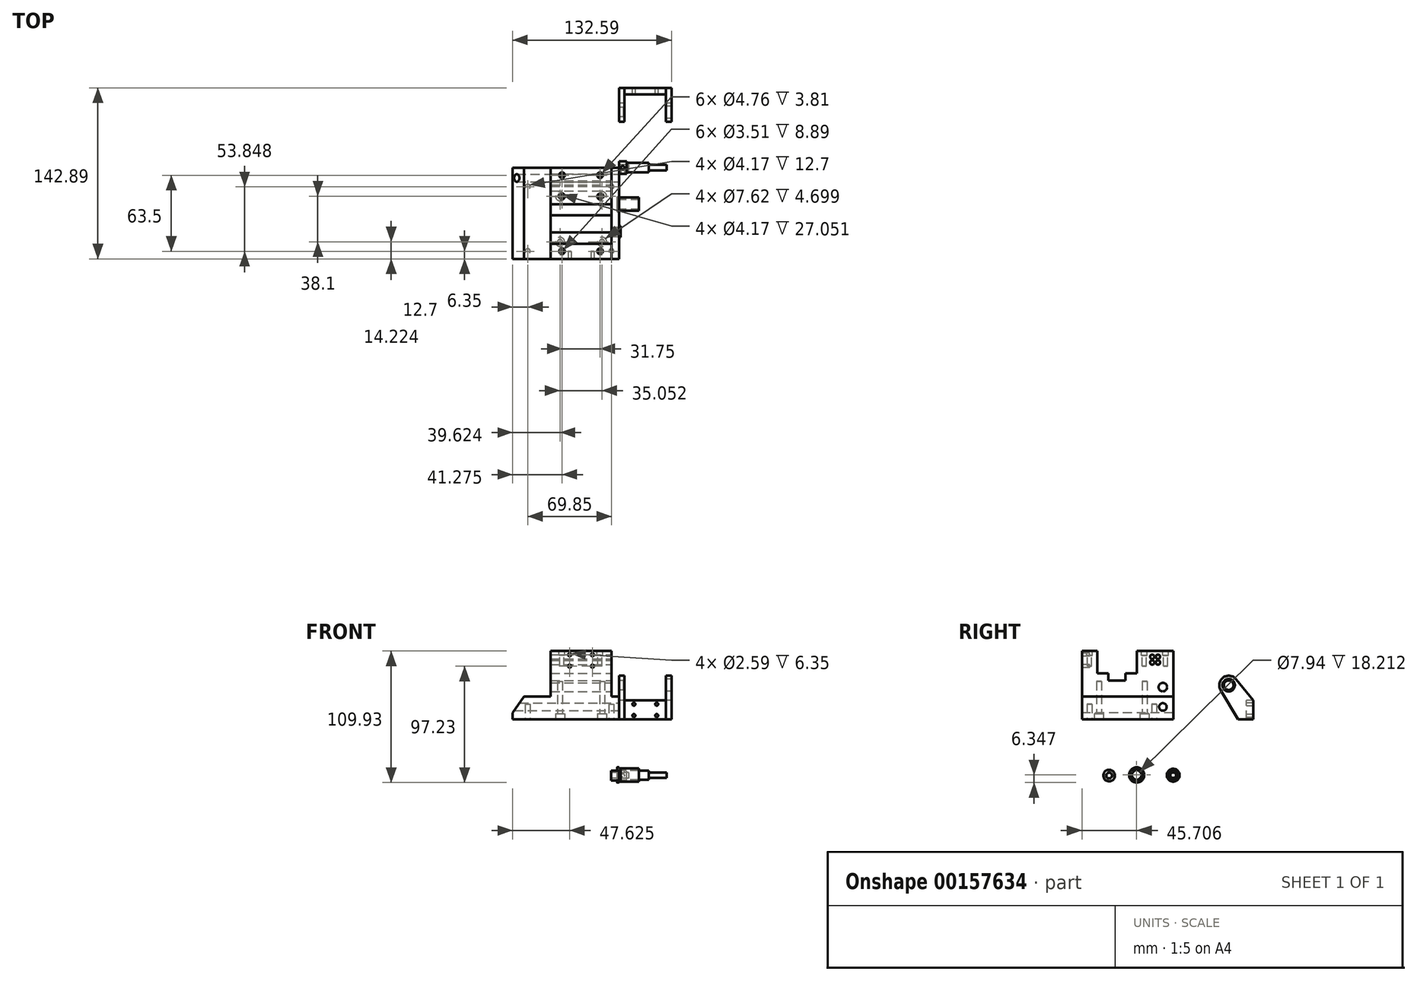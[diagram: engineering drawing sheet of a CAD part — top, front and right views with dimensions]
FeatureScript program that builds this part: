
annotation { "Feature Type Name" : "Feature", "Feature Type Description" : "" }
export const myFeature = defineFeature(function(context is Context, id is Id, definition is map)
    precondition{}
    {
        {
            var Q0;
            Q0=qCreatedBy(makeId("Top.planeOp"),FACE);
            var sketch = newSketch(context, id + "F0", { "sketchPlane" : qUnion([Q0])});
            skLineSegment(sketch, "E0.bottom", {"start": v(0, 0) * mm, "end": v(-88.9, 0) * mm});
            skLineSegment(sketch, "E0.top", {"start": v(0, -76.2) * mm, "end": v(-88.9, -76.2) * mm});
            skLineSegment(sketch, "E0.left", {"start": v(0, 0) * mm, "end": v(0, -76.2) * mm});
            skLineSegment(sketch, "E0.right", {"start": v(-88.9, 0) * mm, "end": v(-88.9, -76.2) * mm});
            skSolve(sketch);
        }
        {
            var Q0;
            Q0=makeQuery(id+"F0.imprint","IMPRINT",FACE,{"disambiguationData":[TD([[makeQuery(id+"F0.imprint","IMPRINT",EDGE,{"derivedFrom":sQuery(id+"F0.wireOp",EDGE,"E0.bottom")}),1.0]])]});
            extrude(context, id + "F1", {"entities" : qUnion([Q0]), "depth" : 19.05 * mm});
        }
        {
            var Q0;
            Q0=makeQuery(id+"F1.opExtrude","CAP_FACE",FACE,{"disambiguationData":[OSD([sQuery(id+"F0.wireOp",EDGE,"E0.bottom"),sQuery(id+"F0.wireOp",EDGE,"E0.top"),sQuery(id+"F0.wireOp",EDGE,"E0.left"),sQuery(id+"F0.wireOp",EDGE,"E0.right")])],"isStart":false});
            var sketch = newSketch(context, id + "F2", { "sketchPlane" : qUnion([Q0])});
            skLineSegment(sketch, "E1", {"start": v(0, 0) * mm, "end": v(-6.35, 0) * mm, "construction": true});
            skLineSegment(sketch, "E2.bottom", {"start": v(-6.35, 0) * mm, "end": v(-57.15, 0) * mm});
            skLineSegment(sketch, "E2.top", {"start": v(-6.35, -76.2) * mm, "end": v(-57.15, -76.2) * mm});
            skLineSegment(sketch, "E2.left", {"start": v(-6.35, 0) * mm, "end": v(-6.35, -76.2) * mm});
            skLineSegment(sketch, "E2.right", {"start": v(-57.15, 0) * mm, "end": v(-57.15, -76.2) * mm});
            skSolve(sketch);
        }
        {
            var Q0;
            Q0=makeQuery(id+"F2.imprint","IMPRINT",FACE,{"disambiguationData":[TD([[makeQuery(id+"F2.imprint","IMPRINT",EDGE,{"derivedFrom":sQuery(id+"F2.wireOp",EDGE,"E2.bottom")}),1.0]])]});
            extrude(context, id + "F3", {"entities" : qUnion([Q0]), "operationType" : NewBodyOperationType.ADD, "depth" : 38.1 * mm});
        }
        {
            var Q0;
            Q0=makeQuery(id+"F3.opExtrude","SWEPT_FACE",FACE,{"disambiguationData":[OSD([sQuery(id+"F2.wireOp",EDGE,"E2.left")])]});
            var sketch = newSketch(context, id + "F4", { "sketchPlane" : qUnion([Q0])});
            skLineSegment(sketch, "E3", {"start": v(-76.2, 57.15) * mm, "end": v(-63.5, 57.15) * mm, "construction": true});
            skLineSegment(sketch, "E4", {"start": v(-54.1, 38.6) * mm, "end": v(-54.1, 35.05) * mm});
            skLineSegment(sketch, "E5", {"start": v(-51.56, 32.51) * mm, "end": v(-42.42, 32.51) * mm});
            skLineSegment(sketch, "E6", {"start": v(-39.88, 35.05) * mm, "end": v(-39.88, 38.6) * mm});
            skLineSegment(sketch, "E7", {"start": v(-30.48, 41.4) * mm, "end": v(-30.48, 57.15) * mm});
            skPoint(sketch, "E8.visualSharp", {"position": v(-54.1, 32.51) * mm});
            skPoint(sketch, "E9.visualSharp", {"position": v(-39.88, 32.51) * mm});
            skLineSegment(sketch, "E10", {"start": v(-63.5, 57.15) * mm, "end": v(-63.5, 41.15) * mm});
            skLineSegment(sketch, "E11", {"start": v(-60.96, 38.6) * mm, "end": v(-54.1, 38.6) * mm});
            skLineSegment(sketch, "E12", {"start": v(-39.88, 38.6) * mm, "end": v(-33.02, 38.6) * mm});
            skLineSegment(sketch, "E13", {"start": v(-30.48, 41.15) * mm, "end": v(-30.48, 41.4) * mm});
            skPoint(sketch, "E14.visualSharp", {"position": v(-63.5, 38.6) * mm});
            skPoint(sketch, "E15.visualSharp", {"position": v(-30.48, 38.6) * mm});
            skLineSegment(sketch, "E16", {"start": v(-33.02, 38.6) * mm, "end": v(-30.48, 38.6) * mm});
            skLineSegment(sketch, "E17", {"start": v(-30.48, 41.15) * mm, "end": v(-30.48, 38.6) * mm});
            skLineSegment(sketch, "E18", {"start": v(-60.96, 38.6) * mm, "end": v(-63.5, 38.6) * mm});
            skLineSegment(sketch, "E19", {"start": v(-63.5, 41.15) * mm, "end": v(-63.5, 38.6) * mm});
            skLineSegment(sketch, "E20", {"start": v(-54.1, 35.05) * mm, "end": v(-54.1, 32.51) * mm});
            skLineSegment(sketch, "E21", {"start": v(-51.56, 32.51) * mm, "end": v(-54.1, 32.51) * mm});
            skLineSegment(sketch, "E22", {"start": v(-42.42, 32.51) * mm, "end": v(-39.88, 32.51) * mm});
            skLineSegment(sketch, "E23", {"start": v(-39.88, 32.51) * mm, "end": v(-39.88, 35.05) * mm});
            skSolve(sketch);
        }
        {
            var Q0;
            Q0=makeQuery(id+"F4.imprint","IMPRINT",FACE,{"disambiguationData":[TD([[makeQuery(id+"F4.imprint","IMPRINT",EDGE,{"derivedFrom":sQuery(id+"F4.wireOp",EDGE,"E4")}),1.0]])]});
            extrude(context, id + "F5", {"entities" : qUnion([Q0]), "operationType" : NewBodyOperationType.REMOVE, "endBound" : BoundingType.THROUGH_ALL, "oppositeDirection" : true, "depth" : 25.4 * mm});
        }
        {
            var Q0;
            Q0=makeQuery(id+"F3.boolean.opBoolean","MERGE",FACE,{"derivedFrom":[makeQuery(id+"F1.opExtrude","SWEPT_FACE",FACE,{"disambiguationData":[OSD([sQuery(id+"F0.wireOp",EDGE,"E0.top")])]}),makeQuery(id+"F3.opExtrude","SWEPT_FACE",FACE,{"disambiguationData":[OSD([sQuery(id+"F2.wireOp",EDGE,"E2.top")])]})]});
            var sketch = newSketch(context, id + "F6", { "sketchPlane" : qUnion([Q0])});
            skLineSegment(sketch, "E24", {"start": v(-88.9, 5.34) * mm, "end": v(-79.3, 19.05) * mm});
            skSolve(sketch);
        }
        {
            var Q0;
            {var subQ0=sQuery(id+"F6.wireOp",EDGE,"E24");Q0=makeQuery(id+"F6.imprint","IMPRINT",FACE,{"disambiguationData":[TD([[makeQuery(id+"F6.imprint","IMPRINT",EDGE,{"derivedFrom":subQ0}),1.0]])]});}
            extrude(context, id + "F7", {"entities" : qUnion([Q0]), "operationType" : NewBodyOperationType.REMOVE, "endBound" : BoundingType.THROUGH_ALL, "oppositeDirection" : true, "depth" : 25.4 * mm});
        }
        {
            var Q0;
            Q0=makeQuery(id+"F1.opExtrude","SWEPT_FACE",FACE,{"disambiguationData":[OSD([sQuery(id+"F0.wireOp",EDGE,"E0.left")])]});
            var sketch = newSketch(context, id + "F8", { "sketchPlane" : qUnion([Q0])});
            skCircle(sketch, "E25", {"center": v(-8.64, 10.41) * mm, "radius": 3.18 * mm});
            skSolve(sketch);
        }
        {
            var Q0;
            Q0=makeQuery(id+"F8.imprint","IMPRINT",FACE,{"disambiguationData":[TD([[makeQuery(id+"F8.imprint","IMPRINT",EDGE,{"derivedFrom":sQuery(id+"F8.wireOp",EDGE,"E25")}),1.0]])]});
            extrude(context, id + "F9", {"entities" : qUnion([Q0]), "operationType" : NewBodyOperationType.REMOVE, "endBound" : BoundingType.THROUGH_ALL, "oppositeDirection" : true, "depth" : 25.4 * mm});
        }
        {
            var Q0;
            Q0=makeQuery(id+"F3.opExtrude","SWEPT_FACE",FACE,{"disambiguationData":[OSD([sQuery(id+"F2.wireOp",EDGE,"E2.left")])]});
            var sketch = newSketch(context, id + "F10", { "sketchPlane" : qUnion([Q0])});
            skCircle(sketch, "E26", {"center": v(-8.64, 26.92) * mm, "radius": 3.56 * mm});
            skSolve(sketch);
        }
        {
            var Q0;
            Q0=makeQuery(id+"F10.imprint","IMPRINT",FACE,{"disambiguationData":[TD([[makeQuery(id+"F10.imprint","IMPRINT",EDGE,{"derivedFrom":sQuery(id+"F10.wireOp",EDGE,"E26")}),1.0]])]});
            extrude(context, id + "F11", {"entities" : qUnion([Q0]), "operationType" : NewBodyOperationType.REMOVE, "endBound" : BoundingType.THROUGH_ALL, "oppositeDirection" : true, "depth" : 25.4 * mm});
        }
        {
            var Q0;
            Q0=makeQuery(id+"F3.opExtrude","SWEPT_FACE",FACE,{"disambiguationData":[OSD([sQuery(id+"F2.wireOp",EDGE,"E2.left")])]});
            var sketch = newSketch(context, id + "F12", { "sketchPlane" : qUnion([Q0])});
            skLineSegment(sketch, "E27.bottom", {"start": v(-17.53, 52.32) * mm, "end": v(-12.7, 52.32) * mm, "construction": true});
            skLineSegment(sketch, "E27.top", {"start": v(-17.53, 47.5) * mm, "end": v(-12.7, 47.5) * mm, "construction": true});
            skLineSegment(sketch, "E27.left", {"start": v(-17.53, 52.32) * mm, "end": v(-17.53, 47.5) * mm, "construction": true});
            skLineSegment(sketch, "E27.right", {"start": v(-12.7, 52.32) * mm, "end": v(-12.7, 47.5) * mm, "construction": true});
            skCircle(sketch, "E28", {"center": v(-12.7, 52.32) * mm, "radius": 1.83 * mm});
            skCircle(sketch, "E29", {"center": v(-17.53, 52.32) * mm, "radius": 1.83 * mm});
            skCircle(sketch, "E30", {"center": v(-17.53, 47.5) * mm, "radius": 1.83 * mm});
            skCircle(sketch, "E31", {"center": v(-12.7, 47.5) * mm, "radius": 1.83 * mm});
            skSolve(sketch);
        }
        {
            var Q0;
            Q0=makeQuery(id+"F12.imprint","IMPRINT",FACE,{"disambiguationData":[TD([[makeQuery(id+"F12.imprint","IMPRINT",EDGE,{"derivedFrom":sQuery(id+"F12.wireOp",EDGE,"E30")}),1.0]])]});
            var Q1;
            Q1=makeQuery(id+"F12.imprint","IMPRINT",FACE,{"disambiguationData":[TD([[makeQuery(id+"F12.imprint","IMPRINT",EDGE,{"derivedFrom":sQuery(id+"F12.wireOp",EDGE,"E31")}),1.0]])]});
            var Q2;
            Q2=makeQuery(id+"F12.imprint","IMPRINT",FACE,{"disambiguationData":[TD([[makeQuery(id+"F12.imprint","IMPRINT",EDGE,{"derivedFrom":sQuery(id+"F12.wireOp",EDGE,"E28")}),1.0]])]});
            var Q3;
            Q3=makeQuery(id+"F12.imprint","IMPRINT",FACE,{"disambiguationData":[TD([[makeQuery(id+"F12.imprint","IMPRINT",EDGE,{"derivedFrom":sQuery(id+"F12.wireOp",EDGE,"E29")}),1.0]])]});
            extrude(context, id + "F13", {"entities" : qUnion([Q0, Q1, Q2, Q3]), "operationType" : NewBodyOperationType.REMOVE, "endBound" : BoundingType.THROUGH_ALL, "oppositeDirection" : true, "depth" : 25.4 * mm});
        }
        {
            var Q0;
            Q0=makeQuery(id+"F1.opExtrude","CAP_FACE",FACE,{"disambiguationData":[OSD([sQuery(id+"F0.wireOp",EDGE,"E0.bottom"),sQuery(id+"F0.wireOp",EDGE,"E0.top"),sQuery(id+"F0.wireOp",EDGE,"E0.left"),sQuery(id+"F0.wireOp",EDGE,"E0.right")])],"isStart":true});
            var sketch = newSketch(context, id + "F14", { "sketchPlane" : qUnion([Q0])});
            skLineSegment(sketch, "E32.bottom", {"start": v(-76.2, 69.85) * mm, "end": v(-6.35, 69.85) * mm, "construction": true});
            skLineSegment(sketch, "E32.top", {"start": v(-76.2, 16) * mm, "end": v(-6.35, 16) * mm, "construction": true});
            skLineSegment(sketch, "E32.left", {"start": v(-76.2, 69.85) * mm, "end": v(-76.2, 16) * mm, "construction": true});
            skLineSegment(sketch, "E32.right", {"start": v(-6.35, 69.85) * mm, "end": v(-6.35, 16) * mm, "construction": true});
            skCircle(sketch, "E33", {"center": v(-6.35, 69.85) * mm, "radius": 2.08 * mm});
            skCircle(sketch, "E34", {"center": v(-76.2, 69.85) * mm, "radius": 2.08 * mm});
            skCircle(sketch, "E35", {"center": v(-76.2, 16) * mm, "radius": 2.08 * mm});
            skCircle(sketch, "E36", {"center": v(-6.35, 16) * mm, "radius": 2.08 * mm});
            skSolve(sketch);
        }
        {
            var Q0;
            Q0=makeQuery(id+"F14.imprint","IMPRINT",FACE,{"disambiguationData":[TD([[makeQuery(id+"F14.imprint","IMPRINT",EDGE,{"derivedFrom":sQuery(id+"F14.wireOp",EDGE,"E34")}),1.0]])]});
            var Q1;
            Q1=makeQuery(id+"F14.imprint","IMPRINT",FACE,{"disambiguationData":[TD([[makeQuery(id+"F14.imprint","IMPRINT",EDGE,{"derivedFrom":sQuery(id+"F14.wireOp",EDGE,"E33")}),1.0]])]});
            var Q2;
            Q2=makeQuery(id+"F14.imprint","IMPRINT",FACE,{"disambiguationData":[TD([[makeQuery(id+"F14.imprint","IMPRINT",EDGE,{"derivedFrom":sQuery(id+"F14.wireOp",EDGE,"E35")}),1.0]])]});
            var Q3;
            Q3=makeQuery(id+"F14.imprint","IMPRINT",FACE,{"disambiguationData":[TD([[makeQuery(id+"F14.imprint","IMPRINT",EDGE,{"derivedFrom":sQuery(id+"F14.wireOp",EDGE,"E36")}),1.0]])]});
            extrude(context, id + "F15", {"entities" : qUnion([Q0, Q1, Q2, Q3]), "operationType" : NewBodyOperationType.REMOVE, "oppositeDirection" : true, "depth" : 12.7 * mm});
        }
        {
            var Q0;
            Q0=makeQuery(id+"F1.opExtrude","CAP_FACE",FACE,{"disambiguationData":[OSD([sQuery(id+"F0.wireOp",EDGE,"E0.bottom"),sQuery(id+"F0.wireOp",EDGE,"E0.top"),sQuery(id+"F0.wireOp",EDGE,"E0.left"),sQuery(id+"F0.wireOp",EDGE,"E0.right")])],"isStart":true});
            var sketch = newSketch(context, id + "F16", { "sketchPlane" : qUnion([Q0])});
            skLineSegment(sketch, "E37.bottom", {"start": v(-49.28, 61.98) * mm, "end": v(-14.22, 61.98) * mm, "construction": true});
            skLineSegment(sketch, "E37.top", {"start": v(-49.28, 23.88) * mm, "end": v(-14.22, 23.88) * mm, "construction": true});
            skLineSegment(sketch, "E37.left", {"start": v(-49.28, 61.98) * mm, "end": v(-49.28, 23.88) * mm, "construction": true});
            skLineSegment(sketch, "E37.right", {"start": v(-14.22, 61.98) * mm, "end": v(-14.22, 23.88) * mm, "construction": true});
            skCircle(sketch, "E38", {"center": v(-14.22, 61.98) * mm, "radius": 2.08 * mm});
            skCircle(sketch, "E39", {"center": v(-49.28, 61.98) * mm, "radius": 2.08 * mm});
            skCircle(sketch, "E40", {"center": v(-49.28, 23.88) * mm, "radius": 2.08 * mm});
            skCircle(sketch, "E41", {"center": v(-14.22, 23.88) * mm, "radius": 2.08 * mm});
            skCircle(sketch, "E42", {"center": v(-14.22, 61.98) * mm, "radius": 3.81 * mm});
            skCircle(sketch, "E43", {"center": v(-49.28, 61.98) * mm, "radius": 3.81 * mm});
            skCircle(sketch, "E44", {"center": v(-49.28, 23.88) * mm, "radius": 3.81 * mm});
            skCircle(sketch, "E45", {"center": v(-14.22, 23.88) * mm, "radius": 3.81 * mm});
            skSolve(sketch);
        }
        {
            var Q0;
            Q0=makeQuery(id+"F16.imprint","IMPRINT",FACE,{"disambiguationData":[TD([[makeQuery(id+"F16.imprint","IMPRINT",EDGE,{"derivedFrom":sQuery(id+"F16.wireOp",EDGE,"E39")}),1.0]])]});
            var Q1;
            Q1=makeQuery(id+"F16.imprint","IMPRINT",FACE,{"disambiguationData":[TD([[makeQuery(id+"F16.imprint","IMPRINT",EDGE,{"derivedFrom":sQuery(id+"F16.wireOp",EDGE,"E38")}),1.0]])]});
            var Q2;
            Q2=makeQuery(id+"F16.imprint","IMPRINT",FACE,{"disambiguationData":[TD([[makeQuery(id+"F16.imprint","IMPRINT",EDGE,{"derivedFrom":sQuery(id+"F16.wireOp",EDGE,"E41")}),1.0]])]});
            var Q3;
            Q3=makeQuery(id+"F16.imprint","IMPRINT",FACE,{"disambiguationData":[TD([[makeQuery(id+"F16.imprint","IMPRINT",EDGE,{"derivedFrom":sQuery(id+"F16.wireOp",EDGE,"E40")}),1.0]])]});
            extrude(context, id + "F17", {"entities" : qUnion([Q0, Q1, Q2, Q3]), "operationType" : NewBodyOperationType.REMOVE, "oppositeDirection" : true, "depth" : 31.75 * mm});
        }
        {
            var Q0;
            Q0=makeQuery(id+"F16.imprint","IMPRINT",FACE,{"disambiguationData":[TD([[makeQuery(id+"F16.imprint","IMPRINT",EDGE,{"derivedFrom":sQuery(id+"F16.wireOp",EDGE,"E39")}),-1.0]])]});
            var Q1;
            Q1=makeQuery(id+"F16.imprint","IMPRINT",FACE,{"disambiguationData":[TD([[makeQuery(id+"F16.imprint","IMPRINT",EDGE,{"derivedFrom":sQuery(id+"F16.wireOp",EDGE,"E38")}),-1.0]])]});
            var Q2;
            Q2=makeQuery(id+"F16.imprint","IMPRINT",FACE,{"disambiguationData":[TD([[makeQuery(id+"F16.imprint","IMPRINT",EDGE,{"derivedFrom":sQuery(id+"F16.wireOp",EDGE,"E41")}),-1.0]])]});
            var Q3;
            Q3=makeQuery(id+"F16.imprint","IMPRINT",FACE,{"disambiguationData":[TD([[makeQuery(id+"F16.imprint","IMPRINT",EDGE,{"derivedFrom":sQuery(id+"F16.wireOp",EDGE,"E40")}),-1.0]])]});
            extrude(context, id + "F18", {"entities" : qUnion([Q0, Q1, Q2, Q3]), "operationType" : NewBodyOperationType.REMOVE, "oppositeDirection" : true, "depth" : 4.7 * mm});
        }
        {
            var Q0;
            Q0=makeQuery(id+"F3.boolean.opBoolean","MERGE",FACE,{"derivedFrom":[makeQuery(id+"F1.opExtrude","SWEPT_FACE",FACE,{"disambiguationData":[OSD([sQuery(id+"F0.wireOp",EDGE,"E0.top")])]}),makeQuery(id+"F3.opExtrude","SWEPT_FACE",FACE,{"disambiguationData":[OSD([sQuery(id+"F2.wireOp",EDGE,"E2.top")])]})]});
            var sketch = newSketch(context, id + "F19", { "sketchPlane" : qUnion([Q0])});
            skLineSegment(sketch, "E46.bottom", {"start": v(-41.28, 53.98) * mm, "end": v(-22.23, 53.98) * mm, "construction": true});
            skLineSegment(sketch, "E46.top", {"start": v(-41.28, 44.45) * mm, "end": v(-22.23, 44.45) * mm, "construction": true});
            skLineSegment(sketch, "E46.left", {"start": v(-41.28, 53.98) * mm, "end": v(-41.28, 44.45) * mm, "construction": true});
            skLineSegment(sketch, "E46.right", {"start": v(-22.23, 53.98) * mm, "end": v(-22.23, 44.45) * mm, "construction": true});
            skCircle(sketch, "E47", {"center": v(-22.23, 53.98) * mm, "radius": 1.3 * mm});
            skCircle(sketch, "E48", {"center": v(-41.28, 53.98) * mm, "radius": 1.3 * mm});
            skCircle(sketch, "E49", {"center": v(-41.28, 44.45) * mm, "radius": 1.3 * mm});
            skCircle(sketch, "E50", {"center": v(-22.23, 44.45) * mm, "radius": 1.3 * mm});
            skSolve(sketch);
        }
        {
            var Q0;
            Q0=makeQuery(id+"F19.imprint","IMPRINT",FACE,{"disambiguationData":[TD([[makeQuery(id+"F19.imprint","IMPRINT",EDGE,{"derivedFrom":sQuery(id+"F19.wireOp",EDGE,"E49")}),1.0]])]});
            var Q1;
            Q1=makeQuery(id+"F19.imprint","IMPRINT",FACE,{"disambiguationData":[TD([[makeQuery(id+"F19.imprint","IMPRINT",EDGE,{"derivedFrom":sQuery(id+"F19.wireOp",EDGE,"E48")}),1.0]])]});
            var Q2;
            Q2=makeQuery(id+"F19.imprint","IMPRINT",FACE,{"disambiguationData":[TD([[makeQuery(id+"F19.imprint","IMPRINT",EDGE,{"derivedFrom":sQuery(id+"F19.wireOp",EDGE,"E47")}),1.0]])]});
            var Q3;
            Q3=makeQuery(id+"F19.imprint","IMPRINT",FACE,{"disambiguationData":[TD([[makeQuery(id+"F19.imprint","IMPRINT",EDGE,{"derivedFrom":sQuery(id+"F19.wireOp",EDGE,"E50")}),1.0]])]});
            extrude(context, id + "F20", {"entities" : qUnion([Q0, Q1, Q2, Q3]), "operationType" : NewBodyOperationType.REMOVE, "oppositeDirection" : true, "depth" : 6.35 * mm});
        }
        {
            var Q0;
            {var subQ0=sQuery(id+"F2.wireOp",EDGE,"E2.right");var subQ1=sQuery(id+"F2.wireOp",EDGE,"E2.left");var subQ2=sQuery(id+"F2.wireOp",EDGE,"E2.bottom");Q0=makeQuery(id+"F5.boolean.opBoolean","SPLIT",FACE,{"disambiguationData":[TD([makeQuery(id+"F1.opExtrude","SWEPT_FACE",FACE,{"disambiguationData":[OSD([sQuery(id+"F0.wireOp",EDGE,"E0.bottom")])]})])],"derivedFrom":makeQuery(id+"F3.opExtrude","CAP_FACE",FACE,{"disambiguationData":[OSD([subQ2,sQuery(id+"F2.wireOp",EDGE,"E2.top"),subQ1,subQ0])],"isStart":false})});}
            var sketch = newSketch(context, id + "F21", { "sketchPlane" : qUnion([Q0])});
            skLineSegment(sketch, "E51.bottom", {"start": v(-47.62, -6.35) * mm, "end": v(-15.88, -6.35) * mm, "construction": true});
            skLineSegment(sketch, "E51.top", {"start": v(-47.62, -24.13) * mm, "end": v(-15.88, -24.13) * mm, "construction": true});
            skLineSegment(sketch, "E51.left", {"start": v(-47.62, -6.35) * mm, "end": v(-47.62, -24.13) * mm, "construction": true});
            skLineSegment(sketch, "E51.right", {"start": v(-15.88, -6.35) * mm, "end": v(-15.88, -24.13) * mm, "construction": true});
            skCircle(sketch, "E52", {"center": v(-47.62, -6.35) * mm, "radius": 1.75 * mm});
            skCircle(sketch, "E53", {"center": v(-15.88, -6.35) * mm, "radius": 1.75 * mm});
            skCircle(sketch, "E54", {"center": v(-47.62, -24.13) * mm, "radius": 1.75 * mm});
            skCircle(sketch, "E55", {"center": v(-15.88, -24.13) * mm, "radius": 1.75 * mm});
            skCircle(sketch, "E56", {"center": v(-15.88, -6.35) * mm, "radius": 2.38 * mm});
            skCircle(sketch, "E57", {"center": v(-15.88, -24.13) * mm, "radius": 2.38 * mm});
            skCircle(sketch, "E58", {"center": v(-47.62, -6.35) * mm, "radius": 2.38 * mm});
            skCircle(sketch, "E59", {"center": v(-47.62, -24.13) * mm, "radius": 2.38 * mm});
            skCircle(sketch, "E60", {"center": v(-15.87, -69.85) * mm, "radius": 1.75 * mm});
            skCircle(sketch, "E61", {"center": v(-47.62, -69.85) * mm, "radius": 1.75 * mm});
            skCircle(sketch, "E62", {"center": v(-47.62, -69.85) * mm, "radius": 2.38 * mm});
            skCircle(sketch, "E63", {"center": v(-15.87, -69.85) * mm, "radius": 2.38 * mm});
            skSolve(sketch);
        }
        {
            var Q0;
            Q0=makeQuery(id+"F21.imprint","IMPRINT",FACE,{"disambiguationData":[TD([[makeQuery(id+"F21.imprint","IMPRINT",EDGE,{"derivedFrom":sQuery(id+"F21.wireOp",EDGE,"E52")}),1.0]])]});
            var Q1;
            Q1=makeQuery(id+"F21.imprint","IMPRINT",FACE,{"disambiguationData":[TD([[makeQuery(id+"F21.imprint","IMPRINT",EDGE,{"derivedFrom":sQuery(id+"F21.wireOp",EDGE,"E53")}),1.0]])]});
            var Q2;
            Q2=makeQuery(id+"F21.imprint","IMPRINT",FACE,{"disambiguationData":[TD([[makeQuery(id+"F21.imprint","IMPRINT",EDGE,{"derivedFrom":sQuery(id+"F21.wireOp",EDGE,"E55")}),1.0]])]});
            var Q3;
            Q3=makeQuery(id+"F21.imprint","IMPRINT",FACE,{"disambiguationData":[TD([[makeQuery(id+"F21.imprint","IMPRINT",EDGE,{"derivedFrom":sQuery(id+"F21.wireOp",EDGE,"E54")}),1.0]])]});
            var Q4;
            Q4=makeQuery(id+"F21.imprint","IMPRINT",FACE,{"disambiguationData":[TD([[makeQuery(id+"F21.imprint","IMPRINT",EDGE,{"derivedFrom":sQuery(id+"F21.wireOp",EDGE,"E61")}),1.0]])]});
            var Q5;
            Q5=makeQuery(id+"F21.imprint","IMPRINT",FACE,{"disambiguationData":[TD([[makeQuery(id+"F21.imprint","IMPRINT",EDGE,{"derivedFrom":sQuery(id+"F21.wireOp",EDGE,"E60")}),1.0]])]});
            extrude(context, id + "F22", {"entities" : qUnion([Q0, Q1, Q2, Q3, Q4, Q5]), "operationType" : NewBodyOperationType.REMOVE, "oppositeDirection" : true, "depth" : 12.7 * mm});
        }
        {
            var Q0;
            Q0=makeQuery(id+"F21.imprint","IMPRINT",FACE,{"disambiguationData":[TD([[makeQuery(id+"F21.imprint","IMPRINT",EDGE,{"derivedFrom":sQuery(id+"F21.wireOp",EDGE,"E52")}),-1.0]])]});
            var Q1;
            Q1=makeQuery(id+"F21.imprint","IMPRINT",FACE,{"disambiguationData":[TD([[makeQuery(id+"F21.imprint","IMPRINT",EDGE,{"derivedFrom":sQuery(id+"F21.wireOp",EDGE,"E53")}),-1.0]])]});
            var Q2;
            Q2=makeQuery(id+"F21.imprint","IMPRINT",FACE,{"disambiguationData":[TD([[makeQuery(id+"F21.imprint","IMPRINT",EDGE,{"derivedFrom":sQuery(id+"F21.wireOp",EDGE,"E55")}),-1.0]])]});
            var Q3;
            Q3=makeQuery(id+"F21.imprint","IMPRINT",FACE,{"disambiguationData":[TD([[makeQuery(id+"F21.imprint","IMPRINT",EDGE,{"derivedFrom":sQuery(id+"F21.wireOp",EDGE,"E54")}),-1.0]])]});
            var Q4;
            Q4=makeQuery(id+"F21.imprint","IMPRINT",FACE,{"disambiguationData":[TD([[makeQuery(id+"F21.imprint","IMPRINT",EDGE,{"derivedFrom":sQuery(id+"F21.wireOp",EDGE,"E61")}),-1.0]])]});
            var Q5;
            Q5=makeQuery(id+"F21.imprint","IMPRINT",FACE,{"disambiguationData":[TD([[makeQuery(id+"F21.imprint","IMPRINT",EDGE,{"derivedFrom":sQuery(id+"F21.wireOp",EDGE,"E60")}),-1.0]])]});
            extrude(context, id + "F23", {"entities" : qUnion([Q0, Q1, Q2, Q3, Q4, Q5]), "operationType" : NewBodyOperationType.REMOVE, "oppositeDirection" : true, "depth" : 3.8 * mm});
        }
        {
            var Q0;
            Q0=qCreatedBy(makeId("Right.planeOp"),FACE);
            var sketch = newSketch(context, id + "F24", { "sketchPlane" : qUnion([Q0])});
            skLineSegment(sketch, "E64", {"start": v(66.69, 0) * mm, "end": v(66.69, -4.8) * mm});
            skCircle(sketch, "E65", {"center": v(46.32, 28.58) * mm, "radius": 3.97 * mm});
            skArc(sketch, "E66", {"start": v(52.44, 33.52) * mm, "mid": v(41.84, 35.05) * mm, "end": v(39.53, 24.58) * mm});
            skLineSegment(sketch, "E67", {"start": v(66.69, 0) * mm, "end": v(53.99, 0) * mm});
            skLineSegment(sketch, "E68", {"start": v(53.99, 0) * mm, "end": v(39.53, 24.58) * mm});
            skLineSegment(sketch, "E69", {"start": v(66.69, 0) * mm, "end": v(66.69, 15.88) * mm});
            skLineSegment(sketch, "E70", {"start": v(66.69, 15.88) * mm, "end": v(52.44, 33.52) * mm});
            skSolve(sketch);
        }
        {
            var Q0;
            Q0=makeQuery(id+"F24.imprint","IMPRINT",FACE,{"disambiguationData":[TD([[makeQuery(id+"F24.imprint","IMPRINT",EDGE,{"derivedFrom":sQuery(id+"F24.wireOp",EDGE,"E65")}),-1.0]])]});
            extrude(context, id + "F25", {"entities" : qUnion([Q0]), "depth" : 4.32 * mm});
        }
        {
            var Q0;
            Q0=makeQuery(id+"F25.opExtrude","CAP_FACE",FACE,{"disambiguationData":[OSD([sQuery(id+"F24.wireOp",EDGE,"E65"),sQuery(id+"F24.wireOp",EDGE,"E66"),sQuery(id+"F24.wireOp",EDGE,"E67"),sQuery(id+"F24.wireOp",EDGE,"E68"),sQuery(id+"F24.wireOp",EDGE,"E69"),sQuery(id+"F24.wireOp",EDGE,"E70")])],"isStart":false});
            var sketch = newSketch(context, id + "F26", { "sketchPlane" : qUnion([Q0])});
            skLineSegment(sketch, "E71.bottom", {"start": v(66.69, 0) * mm, "end": v(61.1, 0) * mm});
            skLineSegment(sketch, "E71.top", {"start": v(66.69, 15.88) * mm, "end": v(61.1, 15.88) * mm});
            skLineSegment(sketch, "E71.left", {"start": v(66.69, 0) * mm, "end": v(66.69, 15.88) * mm});
            skLineSegment(sketch, "E71.right", {"start": v(61.1, 0) * mm, "end": v(61.1, 15.88) * mm});
            skSolve(sketch);
        }
        {
            var Q0;
            Q0=makeQuery(id+"F26.imprint","IMPRINT",FACE,{"disambiguationData":[TD([[makeQuery(id+"F26.imprint","IMPRINT",EDGE,{"derivedFrom":sQuery(id+"F26.wireOp",EDGE,"E71.bottom")}),-1.0]])]});
            extrude(context, id + "F27", {"entities" : qUnion([Q0]), "operationType" : NewBodyOperationType.ADD, "depth" : 34.67 * mm});
        }
        {
            var Q0;
            Q0=makeQuery(id+"F27.opExtrude","CAP_FACE",FACE,{"disambiguationData":[OSD([sQuery(id+"F26.wireOp",EDGE,"E71.bottom"),sQuery(id+"F26.wireOp",EDGE,"E71.top"),sQuery(id+"F26.wireOp",EDGE,"E71.left"),sQuery(id+"F26.wireOp",EDGE,"E71.right")])],"isStart":false});
            var sketch = newSketch(context, id + "F28", { "sketchPlane" : qUnion([Q0])});
            skCircle(sketch, "E72", {"center": v(46.32, 28.58) * mm, "radius": 5.16 * mm});
            skArc(sketch, "E73", {"start": v(52.44, 33.52) * mm, "mid": v(41.84, 35.05) * mm, "end": v(39.53, 24.58) * mm});
            skLineSegment(sketch, "E74", {"start": v(66.69, 0) * mm, "end": v(53.99, 0) * mm});
            skPoint(sketch, "E74.endSnap0", {"position": v(63.9, 0) * mm});
            skLineSegment(sketch, "E75", {"start": v(53.99, 0) * mm, "end": v(39.53, 24.58) * mm});
            skLineSegment(sketch, "E76", {"start": v(66.69, 0) * mm, "end": v(66.69, 15.88) * mm});
            skLineSegment(sketch, "E77", {"start": v(66.69, 15.88) * mm, "end": v(52.44, 33.52) * mm});
            skSolve(sketch);
        }
        {
            var Q0;
            Q0=makeQuery(id+"F28.imprint","IMPRINT",FACE,{"disambiguationData":[TD([[makeQuery(id+"F28.imprint","IMPRINT",EDGE,{"derivedFrom":sQuery(id+"F28.wireOp",EDGE,"E72")}),-1.0]])]});
            var Q1;
            {var subQ0=sQuery(id+"F28.wireOp",EDGE,"E76");Q1=makeQuery(id+"F28.imprint","IMPRINT",FACE,{"disambiguationData":[TD([[makeQuery(id+"F28.imprint","IMPRINT",EDGE,{"derivedFrom":subQ0}),1.0]])]});}
            extrude(context, id + "F29", {"entities" : qUnion([Q0, Q1]), "operationType" : NewBodyOperationType.ADD, "depth" : 4.7 * mm});
        }
        {
            var Q0;
            Q0=makeQuery(id+"F29.boolean.opBoolean","MERGE",FACE,{"derivedFrom":[makeQuery(id+"F27.boolean.opBoolean","MERGE",FACE,{"derivedFrom":[makeQuery(id+"F25.opExtrude","SWEPT_FACE",FACE,{"disambiguationData":[OSD([sQuery(id+"F24.wireOp",EDGE,"E69")])]}),makeQuery(id+"F27.opExtrude","SWEPT_FACE",FACE,{"disambiguationData":[OSD([sQuery(id+"F26.wireOp",EDGE,"E71.left")])]})]}),makeQuery(id+"F29.opExtrude","SWEPT_FACE",FACE,{"disambiguationData":[OSD([sQuery(id+"F28.wireOp",EDGE,"E76")])]})]});
            var sketch = newSketch(context, id + "F30", { "sketchPlane" : qUnion([Q0])});
            skLineSegment(sketch, "E78", {"start": v(-21.84, 0) * mm, "end": v(-21.84, 3.18) * mm, "construction": true});
            skLineSegment(sketch, "E79", {"start": v(-21.84, 3.18) * mm, "end": v(-31.37, 3.18) * mm, "construction": true});
            skLineSegment(sketch, "E80", {"start": v(-31.37, 3.18) * mm, "end": v(-31.37, 12.7) * mm, "construction": true});
            skLineSegment(sketch, "E81", {"start": v(-31.37, 12.7) * mm, "end": v(-12.32, 12.7) * mm, "construction": true});
            skLineSegment(sketch, "E82", {"start": v(-12.32, 12.7) * mm, "end": v(-12.32, 3.18) * mm, "construction": true});
            skCircle(sketch, "E83", {"center": v(-31.37, 12.7) * mm, "radius": 1.27 * mm});
            skCircle(sketch, "E84", {"center": v(-31.37, 3.18) * mm, "radius": 1.27 * mm});
            skCircle(sketch, "E85", {"center": v(-12.32, 12.7) * mm, "radius": 1.27 * mm});
            skCircle(sketch, "E86", {"center": v(-12.32, 3.18) * mm, "radius": 1.27 * mm});
            skSolve(sketch);
        }
        {
            var Q0;
            Q0=makeQuery(id+"F30.imprint","IMPRINT",FACE,{"disambiguationData":[TD([[makeQuery(id+"F30.imprint","IMPRINT",EDGE,{"derivedFrom":sQuery(id+"F30.wireOp",EDGE,"E83")}),1.0]])]});
            var Q1;
            Q1=makeQuery(id+"F30.imprint","IMPRINT",FACE,{"disambiguationData":[TD([[makeQuery(id+"F30.imprint","IMPRINT",EDGE,{"derivedFrom":sQuery(id+"F30.wireOp",EDGE,"E84")}),1.0]])]});
            var Q2;
            Q2=makeQuery(id+"F30.imprint","IMPRINT",FACE,{"disambiguationData":[TD([[makeQuery(id+"F30.imprint","IMPRINT",EDGE,{"derivedFrom":sQuery(id+"F30.wireOp",EDGE,"E85")}),1.0]])]});
            var Q3;
            Q3=makeQuery(id+"F30.imprint","IMPRINT",FACE,{"disambiguationData":[TD([[makeQuery(id+"F30.imprint","IMPRINT",EDGE,{"derivedFrom":sQuery(id+"F30.wireOp",EDGE,"E86")}),1.0]])]});
            extrude(context, id + "F31", {"entities" : qUnion([Q0, Q1, Q2, Q3]), "operationType" : NewBodyOperationType.REMOVE, "oppositeDirection" : true, "depth" : 25.4 * mm});
        }
        {
            var Q0;
            Q0=makeQuery(id+"F25.opExtrude","CAP_EDGE",EDGE,{"disambiguationData":[OSD([sQuery(id+"F24.wireOp",EDGE,"E65")])],"isStart":false});
            var Q1;
            Q1=makeQuery(id+"F29.opExtrude","CAP_EDGE",EDGE,{"disambiguationData":[OSD([sQuery(id+"F28.wireOp",EDGE,"E72")])],"isStart":true});
            chamfer(context, id + "F32", {"entities" : qUnion([Q0, Q1]), "width" : 0.5 * mm, "tangentPropagation" : true});
        }
        {
            var Q0;
            Q0=qCreatedBy(makeId("Right.planeOp"),FACE);
            var sketch = newSketch(context, id + "F33", { "sketchPlane" : qUnion([Q0])});
            skCircle(sketch, "E87", {"center": v(-53.5, -46.94) * mm, "radius": 4.83 * mm});
            skSolve(sketch);
        }
        {
            var Q0;
            Q0=makeQuery(id+"F33.imprint","IMPRINT",FACE,{"disambiguationData":[TD([[makeQuery(id+"F33.imprint","IMPRINT",EDGE,{"derivedFrom":sQuery(id+"F33.wireOp",EDGE,"E87")}),1.0]])]});
            extrude(context, id + "F34", {"entities" : qUnion([Q0]), "depth" : 1.27 * mm});
        }
        {
            var Q0;
            Q0=makeQuery(id+"F34.opExtrude","CAP_FACE",FACE,{"disambiguationData":[OSD([sQuery(id+"F33.wireOp",EDGE,"E87")])],"isStart":true});
            var sketch = newSketch(context, id + "F35", { "sketchPlane" : qUnion([Q0])});
            skCircle(sketch, "E88", {"center": v(53.5, -46.94) * mm, "radius": 3.98 * mm});
            skSolve(sketch);
        }
        {
            var Q0;
            Q0=makeQuery(id+"F35.imprint","IMPRINT",FACE,{"disambiguationData":[TD([[makeQuery(id+"F35.imprint","IMPRINT",EDGE,{"derivedFrom":sQuery(id+"F35.wireOp",EDGE,"E88")}),1.0]])]});
            extrude(context, id + "F36", {"entities" : qUnion([Q0]), "operationType" : NewBodyOperationType.ADD, "depth" : 6.6 * mm});
        }
        {
            var Q0;
            Q0=makeQuery(id+"F36.opExtrude","CAP_FACE",FACE,{"disambiguationData":[OSD([sQuery(id+"F35.wireOp",EDGE,"E88")])],"isStart":false});
            var sketch = newSketch(context, id + "F37", { "sketchPlane" : qUnion([Q0])});
            skCircle(sketch, "E89", {"center": v(53.5, -46.94) * mm, "radius": 2.38 * mm});
            skSolve(sketch);
        }
        {
            var Q0;
            Q0=makeQuery(id+"F37.imprint","IMPRINT",FACE,{"disambiguationData":[TD([[makeQuery(id+"F37.imprint","IMPRINT",EDGE,{"derivedFrom":sQuery(id+"F37.wireOp",EDGE,"E89")}),1.0]])]});
            extrude(context, id + "F38", {"entities" : qUnion([Q0]), "operationType" : NewBodyOperationType.REMOVE, "oppositeDirection" : true, "depth" : 25.4 * mm});
        }
        {
            var Q0;
            Q0=qCreatedBy(makeId("Right.planeOp"),FACE);
            var sketch = newSketch(context, id + "F39", { "sketchPlane" : qUnion([Q0])});
            skCircle(sketch, "E90", {"center": v(-30.5, -46.43) * mm, "radius": 6.35 * mm});
            skSolve(sketch);
        }
        {
            var Q0;
            Q0=makeQuery(id+"F39.imprint","IMPRINT",FACE,{"disambiguationData":[TD([[makeQuery(id+"F39.imprint","IMPRINT",EDGE,{"derivedFrom":sQuery(id+"F39.wireOp",EDGE,"E90")}),1.0]])]});
            extrude(context, id + "F40", {"entities" : qUnion([Q0]), "oppositeDirection" : true, "depth" : 1.57 * mm});
        }
        {
            var Q0;
            Q0=makeQuery(id+"F40.opExtrude","CAP_FACE",FACE,{"disambiguationData":[OSD([sQuery(id+"F39.wireOp",EDGE,"E90")])],"isStart":true});
            var sketch = newSketch(context, id + "F41", { "sketchPlane" : qUnion([Q0])});
            skCircle(sketch, "E91", {"center": v(-30.5, -46.43) * mm, "radius": 5.55 * mm});
            skSolve(sketch);
        }
        {
            var Q0;
            Q0=makeQuery(id+"F41.imprint","IMPRINT",FACE,{"disambiguationData":[TD([[makeQuery(id+"F41.imprint","IMPRINT",EDGE,{"derivedFrom":sQuery(id+"F41.wireOp",EDGE,"E91")}),1.0]])]});
            extrude(context, id + "F42", {"entities" : qUnion([Q0]), "operationType" : NewBodyOperationType.ADD, "depth" : 16.64 * mm});
        }
        {
            var Q0;
            Q0=makeQuery(id+"F42.opExtrude","CAP_FACE",FACE,{"disambiguationData":[OSD([sQuery(id+"F41.wireOp",EDGE,"E91")])],"isStart":false});
            var sketch = newSketch(context, id + "F43", { "sketchPlane" : qUnion([Q0])});
            skCircle(sketch, "E92", {"center": v(-30.5, -46.43) * mm, "radius": 3.97 * mm});
            skSolve(sketch);
        }
        {
            var Q0;
            Q0=makeQuery(id+"F43.imprint","IMPRINT",FACE,{"disambiguationData":[TD([[makeQuery(id+"F43.imprint","IMPRINT",EDGE,{"derivedFrom":sQuery(id+"F43.wireOp",EDGE,"E92")}),1.0]])]});
            extrude(context, id + "F44", {"entities" : qUnion([Q0]), "operationType" : NewBodyOperationType.REMOVE, "oppositeDirection" : true, "depth" : 25.4 * mm});
        }
        {
            var Q0;
            Q0=qCreatedBy(makeId("Right.planeOp"),FACE);
            var sketch = newSketch(context, id + "F45", { "sketchPlane" : qUnion([Q0])});
            skCircle(sketch, "E93", {"center": v(0, -46.63) * mm, "radius": 5.33 * mm});
            skSolve(sketch);
        }
        {
            var Q0;
            Q0=makeQuery(id+"F45.imprint","IMPRINT",FACE,{"disambiguationData":[TD([[makeQuery(id+"F45.imprint","IMPRINT",EDGE,{"derivedFrom":sQuery(id+"F45.wireOp",EDGE,"E93")}),1.0]])]});
            extrude(context, id + "F46", {"entities" : qUnion([Q0]), "depth" : 6.35 * mm});
        }
        {
            var Q0;
            Q0=makeQuery(id+"F46.opExtrude","CAP_FACE",FACE,{"disambiguationData":[OSD([sQuery(id+"F45.wireOp",EDGE,"E93")])],"isStart":false});
            var sketch = newSketch(context, id + "F47", { "sketchPlane" : qUnion([Q0])});
            skCircle(sketch, "E94", {"center": v(0, -46.63) * mm, "radius": 3.96 * mm});
            skSolve(sketch);
        }
        {
            var Q0;
            Q0=makeQuery(id+"F47.imprint","IMPRINT",FACE,{"disambiguationData":[TD([[makeQuery(id+"F47.imprint","IMPRINT",EDGE,{"derivedFrom":sQuery(id+"F47.wireOp",EDGE,"E94")}),1.0]])]});
            extrude(context, id + "F48", {"entities" : qUnion([Q0]), "operationType" : NewBodyOperationType.ADD, "depth" : 18.34 * mm});
        }
        {
            var Q0;
            Q0=makeQuery(id+"F48.opExtrude","CAP_FACE",FACE,{"disambiguationData":[OSD([sQuery(id+"F47.wireOp",EDGE,"E94")])],"isStart":false});
            var sketch = newSketch(context, id + "F49", { "sketchPlane" : qUnion([Q0])});
            skCircle(sketch, "E95", {"center": v(0, -46.63) * mm, "radius": 2.37 * mm});
            skSolve(sketch);
        }
        {
            var Q0;
            Q0=makeQuery(id+"F49.imprint","IMPRINT",FACE,{"disambiguationData":[TD([[makeQuery(id+"F49.imprint","IMPRINT",EDGE,{"derivedFrom":sQuery(id+"F49.wireOp",EDGE,"E95")}),1.0]])]});
            extrude(context, id + "F50", {"entities" : qUnion([Q0]), "operationType" : NewBodyOperationType.ADD, "depth" : 15.06 * mm});
        }
        {
            var Q0;
            Q0=makeQuery(id+"F46.opExtrude","CAP_FACE",FACE,{"disambiguationData":[OSD([sQuery(id+"F45.wireOp",EDGE,"E93")])],"isStart":true});
            var sketch = newSketch(context, id + "F51", { "sketchPlane" : qUnion([Q0])});
            skCircle(sketch, "E96", {"center": v(0, -46.63) * mm, "radius": 2.38 * mm});
            skLineSegment(sketch, "E97", {"start": v(0, -46.63) * mm, "end": v(5.33, -46.63) * mm});
            skLineSegment(sketch, "E98", {"start": v(0, -46.63) * mm, "end": v(0, -41.3) * mm});
            skSolve(sketch);
        }
        {
            var Q0;
            Q0=makeQuery(id+"F51.imprint","IMPRINT",FACE,{"disambiguationData":[TD([[makeQuery(id+"F51.imprint","IMPRINT",EDGE,{"derivedFrom":sQuery(id+"F51.wireOp",EDGE,"E96")}),1.0]])]});
            extrude(context, id + "F52", {"entities" : qUnion([Q0]), "operationType" : NewBodyOperationType.REMOVE, "oppositeDirection" : true, "depth" : 7.87 * mm});
        }
        {
            var Q0;
            Q0=qCreatedBy(makeId("Front.planeOp"),FACE);
            var Q1;
            Q1=sQuery(id+"F51.wireOp",VERTEX,"E97.end");
            cPlane(context, id + "F53", {"entities" : qUnion([Q0, Q1]), "cplaneType" : CPlaneType.PLANE_POINT, "offset" : 25.4 * mm, "width" : 152.4 * mm, "height" : 152.4 * mm});
        }
        {
            var Q0;
            Q0=qCreatedBy(id+"F53.planeOp",FACE);
            var sketch = newSketch(context, id + "F54", { "sketchPlane" : qUnion([Q0])});
            skLineSegment(sketch, "E99", {"start": v(0, -46.66) * mm, "end": v(6.29, -46.66) * mm, "construction": true});
            skCircle(sketch, "E100", {"center": v(3.05, -46.66) * mm, "radius": 1.42 * mm});
            skSolve(sketch);
        }
        {
            var Q0;
            Q0=makeQuery(id+"F54.imprint","IMPRINT",FACE,{"disambiguationData":[TD([[makeQuery(id+"F54.imprint","IMPRINT",EDGE,{"derivedFrom":sQuery(id+"F54.wireOp",EDGE,"E100")}),1.0]])]});
            extrude(context, id + "F55", {"entities" : qUnion([Q0]), "operationType" : NewBodyOperationType.REMOVE, "oppositeDirection" : true, "depth" : 5.08 * mm});
        }
        {
            var Q0;
            Q0=qCreatedBy(makeId("Top.planeOp"),FACE);
            var Q1;
            Q1=sQuery(id+"F51.wireOp",VERTEX,"E98.end");
            cPlane(context, id + "F56", {"entities" : qUnion([Q0, Q1]), "cplaneType" : CPlaneType.PLANE_POINT, "offset" : 25.4 * mm, "width" : 152.4 * mm, "height" : 152.4 * mm});
        }
        {
            var Q0;
            Q0=qCreatedBy(id+"F56.planeOp",FACE);
            var sketch = newSketch(context, id + "F57", { "sketchPlane" : qUnion([Q0])});
            skLineSegment(sketch, "E101", {"start": v(0, 0) * mm, "end": v(6.1, 0) * mm, "construction": true});
            skCircle(sketch, "E102", {"center": v(3.05, 0) * mm, "radius": 1.42 * mm});
            skSolve(sketch);
        }
        {
            var Q0;
            Q0=makeQuery(id+"F57.imprint","IMPRINT",FACE,{"disambiguationData":[TD([[makeQuery(id+"F57.imprint","IMPRINT",EDGE,{"derivedFrom":sQuery(id+"F57.wireOp",EDGE,"E102")}),1.0]])]});
            extrude(context, id + "F58", {"entities" : qUnion([Q0]), "operationType" : NewBodyOperationType.REMOVE, "oppositeDirection" : true, "depth" : 5.08 * mm});
        }
    });
